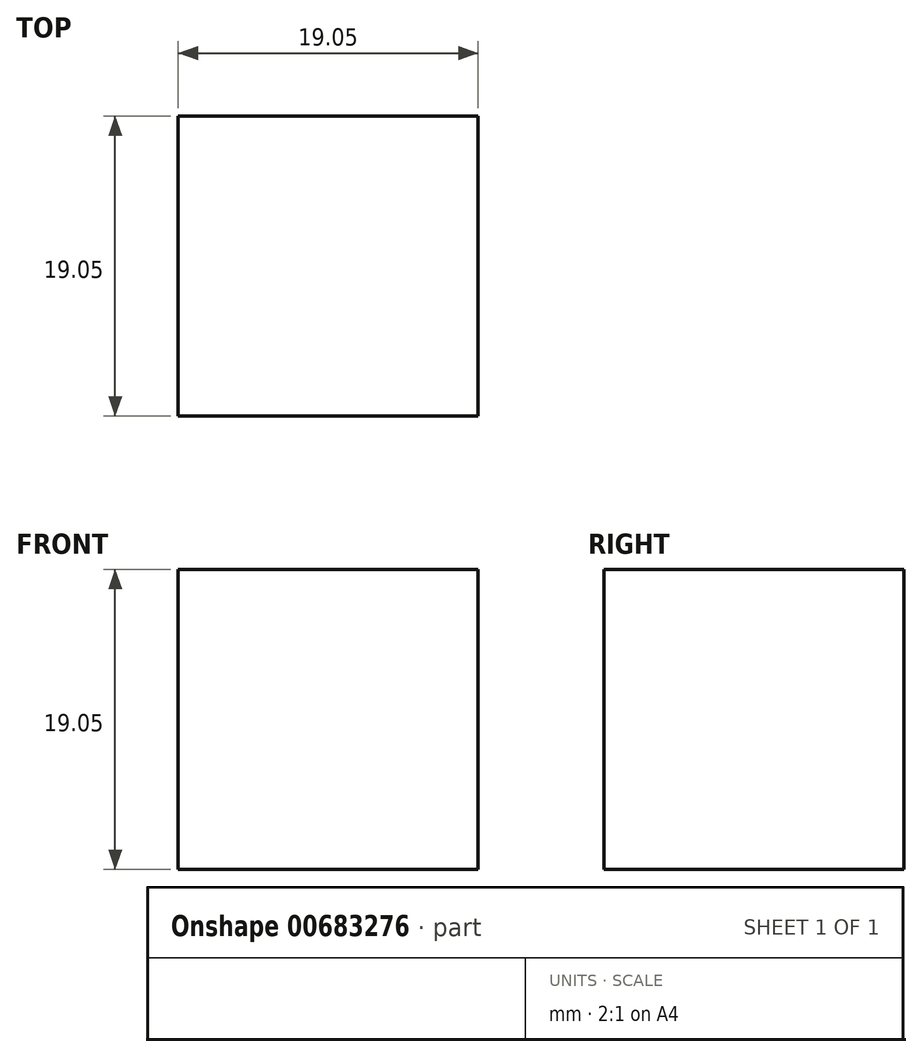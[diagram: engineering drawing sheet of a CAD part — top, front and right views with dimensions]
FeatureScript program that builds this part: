
annotation { "Feature Type Name" : "Feature", "Feature Type Description" : "" }
export const myFeature = defineFeature(function(context is Context, id is Id, definition is map)
    precondition{}
    {
        {
            var Q0;
            Q0=qCreatedBy(makeId("Front.planeOp"),FACE);
            var sketch = newSketch(context, id + "F0", { "sketchPlane" : qUnion([Q0])});
            skLineSegment(sketch, "E0.bottom", {"start": v(-53.07, 66.87) * mm, "end": v(-34.02, 66.87) * mm});
            skLineSegment(sketch, "E0.top", {"start": v(-53.07, 47.82) * mm, "end": v(-34.02, 47.82) * mm});
            skLineSegment(sketch, "E0.left", {"start": v(-53.07, 66.87) * mm, "end": v(-53.07, 47.82) * mm});
            skLineSegment(sketch, "E0.right", {"start": v(-34.02, 66.87) * mm, "end": v(-34.02, 47.82) * mm});
            skSolve(sketch);
        }
        {
            var Q0;
            Q0 = qSketchRegion(id + "F0", true);
            extrude(context, id + "F1", {"entities" : qUnion([Q0]), "depth" : 19.05 * mm, "offsetDistance" : 25.4 * mm});
        }
    });
